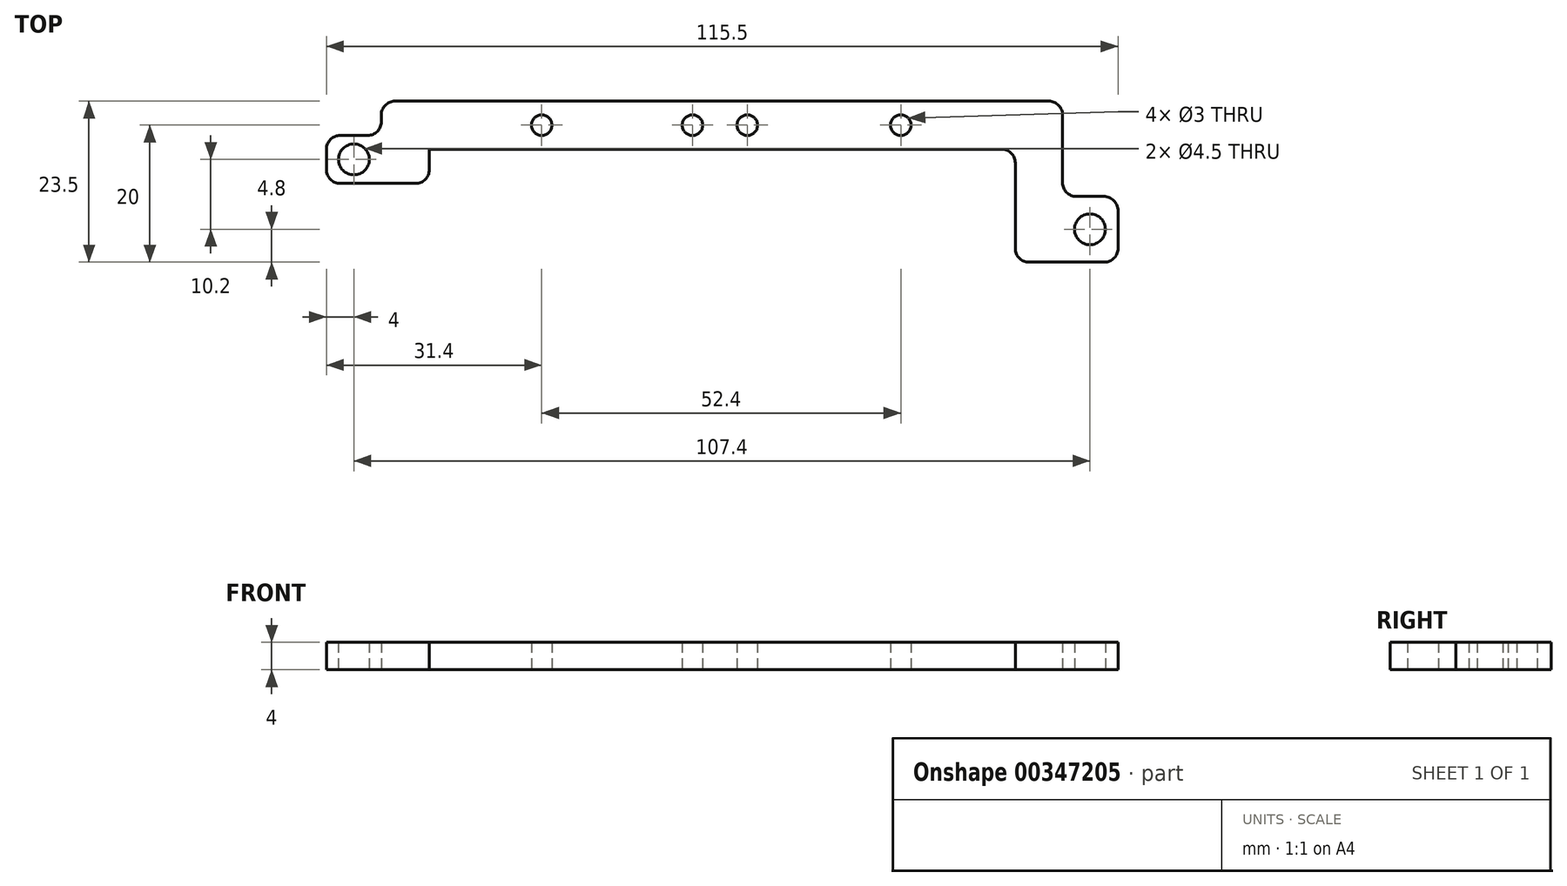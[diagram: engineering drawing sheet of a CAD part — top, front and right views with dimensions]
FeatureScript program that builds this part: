
annotation { "Feature Type Name" : "Feature", "Feature Type Description" : "" }
export const myFeature = defineFeature(function(context is Context, id is Id, definition is map)
    precondition{}
    {
        {
            var Q0;
            Q0=qCreatedBy(makeId("Top.planeOp"),FACE);
            var sketch = newSketch(context, id + "F0", { "sketchPlane" : qUnion([Q0])});
            skLineSegment(sketch, "E0.bottom", {"start": v(57.25, 11) * mm, "end": v(46.25, 11) * mm});
            skPoint(sketch, "E1.orphan", {"position": v(-57.75, 11) * mm});
            skLineSegment(sketch, "E2.MirrorCS", {"start": v(-56.25, 24.5) * mm, "end": v(-56.25, 27.5) * mm});
            skLineSegment(sketch, "E3.MirrorCS", {"start": v(51.15, 22.6) * mm, "end": v(51.15, 32.5) * mm});
            skLineSegment(sketch, "E4.MirrorCS", {"start": v(59.25, 13) * mm, "end": v(59.25, 18.5) * mm});
            skLineSegment(sketch, "E5.MirrorCS", {"start": v(44.25, 13) * mm, "end": v(44.25, 25.5) * mm});
            skLineSegment(sketch, "E6.MirrorCS", {"start": v(49.15, 34.5) * mm, "end": v(-46.25, 34.5) * mm});
            skPoint(sketch, "E7.MirrorP", {"position": v(57.75, 33) * mm});
            skLineSegment(sketch, "E8.MirrorCS", {"start": v(57.15, 20.6) * mm, "end": v(53.15, 20.6) * mm});
            skPoint(sketch, "E9.MirrorP", {"position": v(0, 22) * mm});
            skLineSegment(sketch, "E10.MirrorCS", {"start": v(42.25, 27.5) * mm, "end": v(-41.25, 27.5) * mm});
            skLineSegment(sketch, "E11.0", {"start": v(-41.25, 24.5) * mm, "end": v(-41.25, 27.5) * mm});
            skLineSegment(sketch, "E12.0", {"start": v(-50.25, 29.5) * mm, "end": v(-54.25, 29.5) * mm});
            skLineSegment(sketch, "E13.trimOffspring", {"start": v(-43.25, 22.5) * mm, "end": v(-54.25, 22.5) * mm});
            skLineSegment(sketch, "E14.trimOffspring", {"start": v(-48.25, 31.5) * mm, "end": v(-48.25, 32.5) * mm});
            skPoint(sketch, "E15.visualSharp", {"position": v(59.25, 11) * mm});
            skArc(sketch, "E15.filletArc", {"start": v(57.25, 11) * mm, "mid": v(58.66, 11.59) * mm, "end": v(59.25, 13) * mm});
            skArc(sketch, "E16.filletArc", {"start": v(44.25, 13) * mm, "mid": v(44.84, 11.59) * mm, "end": v(46.25, 11) * mm});
            skPoint(sketch, "E17.visualSharp", {"position": v(59.25, 20.6) * mm});
            skArc(sketch, "E17.filletArc", {"start": v(59.25, 18.5) * mm, "mid": v(58.63, 19.98) * mm, "end": v(57.15, 20.6) * mm});
            skPoint(sketch, "E18.visualSharp", {"position": v(51.15, 20.6) * mm});
            skArc(sketch, "E18.filletArc", {"start": v(51.15, 22.6) * mm, "mid": v(51.74, 21.19) * mm, "end": v(53.15, 20.6) * mm});
            skPoint(sketch, "E19.visualSharp", {"position": v(51.15, 34.5) * mm});
            skArc(sketch, "E19.filletArc", {"start": v(51.15, 32.5) * mm, "mid": v(50.56, 33.91) * mm, "end": v(49.15, 34.5) * mm});
            skPoint(sketch, "E20.visualSharp", {"position": v(44.25, 27.5) * mm});
            skArc(sketch, "E20.filletArc", {"start": v(44.25, 25.5) * mm, "mid": v(43.66, 26.91) * mm, "end": v(42.25, 27.5) * mm});
            skPoint(sketch, "E21.visualSharp", {"position": v(-48.25, 34.5) * mm});
            skArc(sketch, "E21.filletArc", {"start": v(-46.25, 34.5) * mm, "mid": v(-47.66, 33.91) * mm, "end": v(-48.25, 32.5) * mm});
            skPoint(sketch, "E22.visualSharp", {"position": v(-56.25, 22.5) * mm});
            skArc(sketch, "E22.filletArc", {"start": v(-56.25, 24.5) * mm, "mid": v(-55.66, 23.09) * mm, "end": v(-54.25, 22.5) * mm});
            skPoint(sketch, "E23.visualSharp", {"position": v(-41.25, 22.5) * mm});
            skArc(sketch, "E23.filletArc", {"start": v(-43.25, 22.5) * mm, "mid": v(-41.84, 23.09) * mm, "end": v(-41.25, 24.5) * mm});
            skPoint(sketch, "E24.visualSharp", {"position": v(-56.25, 29.5) * mm});
            skArc(sketch, "E24.filletArc", {"start": v(-54.25, 29.5) * mm, "mid": v(-55.66, 28.91) * mm, "end": v(-56.25, 27.5) * mm});
            skPoint(sketch, "E25.visualSharp", {"position": v(-48.25, 29.5) * mm});
            skArc(sketch, "E25.filletArc", {"start": v(-50.25, 29.5) * mm, "mid": v(-48.84, 30.09) * mm, "end": v(-48.25, 31.5) * mm});
            skLineSegment(sketch, "E26", {"start": v(55.15, 20.6) * mm, "end": v(55.15, 11) * mm, "construction": true});
            skCircle(sketch, "E27", {"center": v(55.15, 15.8) * mm, "radius": 2.25 * mm});
            skLineSegment(sketch, "E28", {"start": v(-52.25, 29.5) * mm, "end": v(-52.25, 22.5) * mm, "construction": true});
            skCircle(sketch, "E29", {"center": v(-52.25, 26) * mm, "radius": 2.25 * mm});
            skLineSegment(sketch, "E30.0", {"start": v(49.15, 31) * mm, "end": v(-46.25, 31) * mm, "construction": true});
            skCircle(sketch, "E31", {"center": v(27.55, 31) * mm, "radius": 1.5 * mm});
            skCircle(sketch, "E32", {"center": v(5.15, 31) * mm, "radius": 1.5 * mm});
            skCircle(sketch, "E33", {"center": v(-2.85, 31) * mm, "radius": 1.5 * mm});
            skCircle(sketch, "E34", {"center": v(-24.85, 31) * mm, "radius": 1.5 * mm});
            skSolve(sketch);
        }
        {
            var Q0;
            Q0 = qSketchRegion(id + "F0", true);
            extrude(context, id + "F1", {"entities" : qUnion([Q0]), "endBound" : BoundingType.SYMMETRIC, "depth" : 4 * mm});
        }
    });
